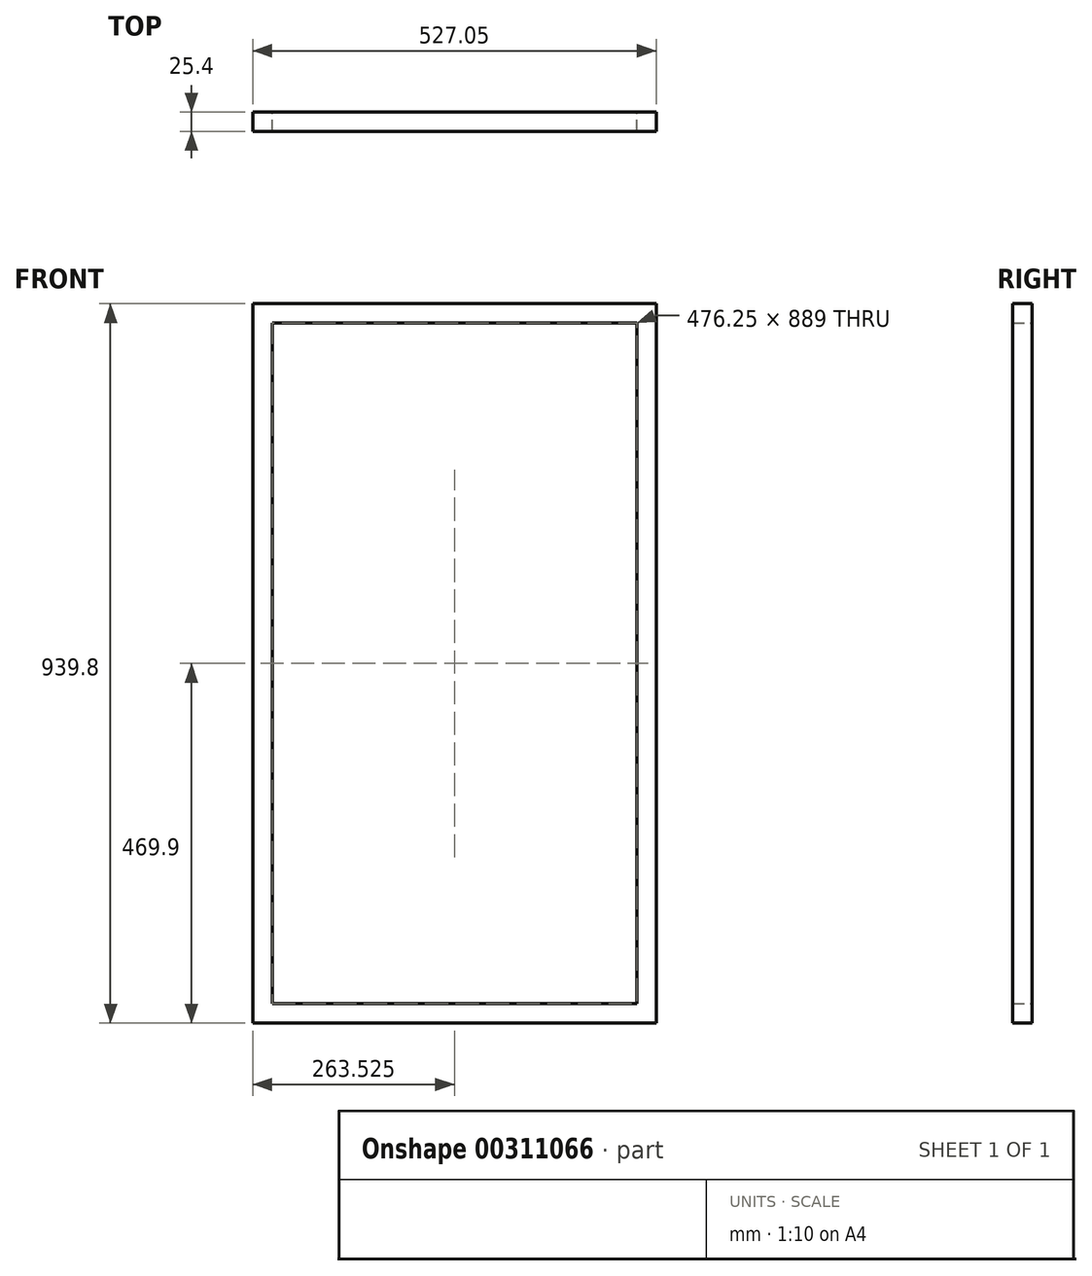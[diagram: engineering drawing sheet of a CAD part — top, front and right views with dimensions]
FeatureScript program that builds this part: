
annotation { "Feature Type Name" : "Feature", "Feature Type Description" : "" }
export const myFeature = defineFeature(function(context is Context, id is Id, definition is map)
    precondition{}
    {
        {
            var Q0;
            Q0=qCreatedBy(makeId("Front.planeOp"),FACE);
            var sketch = newSketch(context, id + "F0", { "sketchPlane" : qUnion([Q0])});
            skLineSegment(sketch, "E0.bottom", {"start": v(0, 0) * mm, "end": v(527.05, 0) * mm});
            skLineSegment(sketch, "E0.top", {"start": v(0, 939.8) * mm, "end": v(527.05, 939.8) * mm});
            skLineSegment(sketch, "E0.left", {"start": v(0, 0) * mm, "end": v(0, 939.8) * mm});
            skLineSegment(sketch, "E0.right", {"start": v(527.05, 0) * mm, "end": v(527.05, 939.8) * mm});
            skLineSegment(sketch, "E1.0", {"start": v(25.4, 914.4) * mm, "end": v(501.65, 914.4) * mm});
            skLineSegment(sketch, "E1.1", {"start": v(25.4, 25.4) * mm, "end": v(25.4, 914.4) * mm});
            skLineSegment(sketch, "E1.2", {"start": v(25.4, 25.4) * mm, "end": v(501.65, 25.4) * mm});
            skLineSegment(sketch, "E1.3", {"start": v(501.65, 25.4) * mm, "end": v(501.65, 914.4) * mm});
            skSolve(sketch);
        }
        {
            var Q0;
            Q0 = qSketchRegion(id + "F0", true);
            extrude(context, id + "F1", {"entities" : qUnion([Q0]), "depth" : 25.4 * mm});
        }
    });
